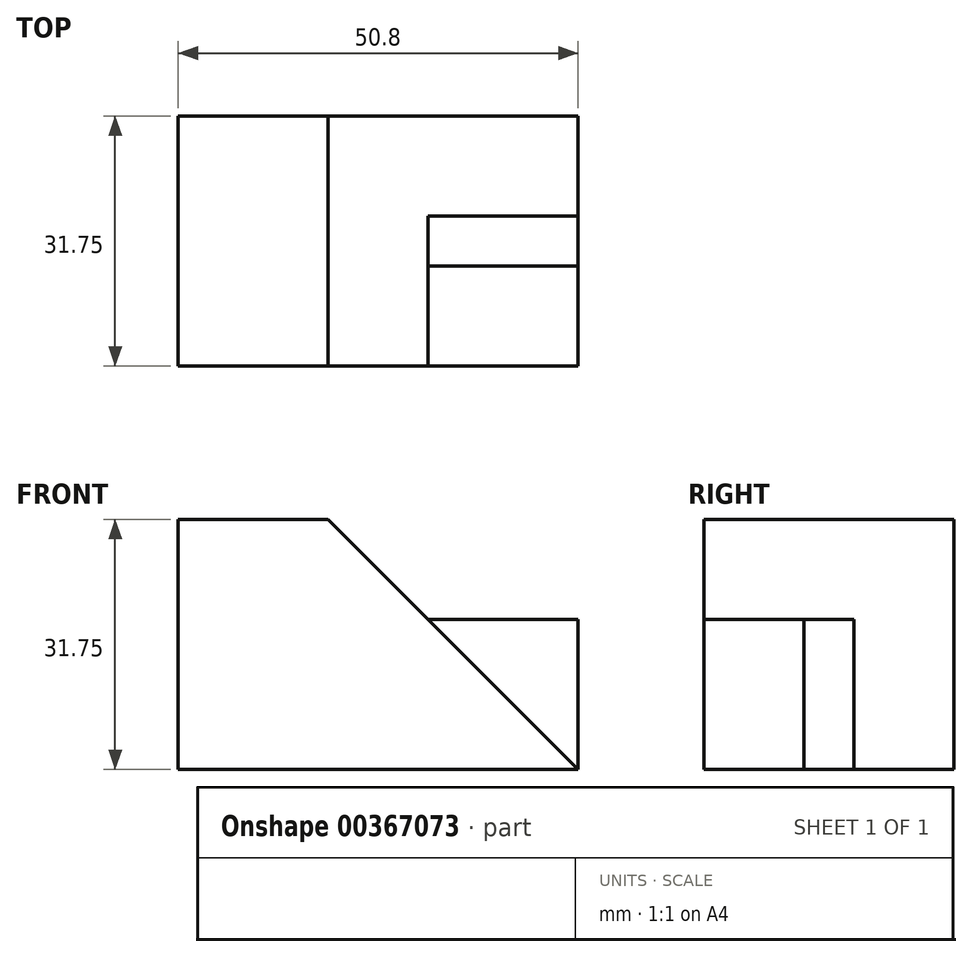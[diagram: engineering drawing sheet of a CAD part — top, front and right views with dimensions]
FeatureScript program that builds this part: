
annotation { "Feature Type Name" : "Feature", "Feature Type Description" : "" }
export const myFeature = defineFeature(function(context is Context, id is Id, definition is map)
    precondition{}
    {
        {
            var Q0;
            Q0=qCreatedBy(makeId("Front.planeOp"),FACE);
            var sketch = newSketch(context, id + "F0", { "sketchPlane" : qUnion([Q0])});
            skLineSegment(sketch, "E0", {"start": v(0, 31.75) * mm, "end": v(19.05, 31.75) * mm});
            skLineSegment(sketch, "E1", {"start": v(19.05, 31.75) * mm, "end": v(50.8, 0) * mm});
            skLineSegment(sketch, "E2", {"start": v(50.8, 0) * mm, "end": v(0, 0) * mm});
            skLineSegment(sketch, "E3", {"start": v(0, 31.75) * mm, "end": v(0, 0) * mm});
            skSolve(sketch);
        }
        {
            var Q0;
            Q0 = qSketchRegion(id + "F0", true);
            extrude(context, id + "F1", {"entities" : qUnion([Q0]), "depth" : 31.75 * mm});
        }
        {
            var Q0;
            Q0=makeQuery(id+"F1.opExtrude","CAP_FACE",FACE,{"disambiguationData":[OSD([sQuery(id+"F0.wireOp",EDGE,"E0"),sQuery(id+"F0.wireOp",EDGE,"E1"),sQuery(id+"F0.wireOp",EDGE,"E2"),sQuery(id+"F0.wireOp",EDGE,"E3")])],"isStart":false});
            var sketch = newSketch(context, id + "F2", { "sketchPlane" : qUnion([Q0])});
            skLineSegment(sketch, "E4", {"start": v(31.75, 19.05) * mm, "end": v(50.8, 19.05) * mm});
            skLineSegment(sketch, "E5", {"start": v(50.8, 19.05) * mm, "end": v(50.8, 0) * mm});
            skLineSegment(sketch, "E6", {"start": v(50.8, 0) * mm, "end": v(31.75, 19.05) * mm});
            skSolve(sketch);
        }
        {
            var Q0;
            Q0 = qSketchRegion(id + "F2", true);
            extrude(context, id + "F3", {"entities" : qUnion([Q0]), "oppositeDirection" : true, "depth" : 19.05 * mm});
        }
        {
            var Q0;
            Q0=makeQuery(id+"F3.opExtrude","CAP_FACE",FACE,{"disambiguationData":[OSD([sQuery(id+"F2.wireOp",EDGE,"E4"),sQuery(id+"F2.wireOp",EDGE,"E5"),sQuery(id+"F2.wireOp",EDGE,"E6")])],"isStart":true});
            var sketch = newSketch(context, id + "F4", { "sketchPlane" : qUnion([Q0])});
            skLineSegment(sketch, "E7", {"start": v(31.75, 19.05) * mm, "end": v(50.8, 19.05) * mm});
            skLineSegment(sketch, "E8", {"start": v(50.8, 19.05) * mm, "end": v(50.8, 0) * mm});
            skLineSegment(sketch, "E9", {"start": v(50.8, 0) * mm, "end": v(31.75, 19.05) * mm});
            skSolve(sketch);
        }
        {
            var Q0;
            Q0 = qSketchRegion(id + "F4", true);
            extrude(context, id + "F5", {"entities" : qUnion([Q0]), "oppositeDirection" : true, "depth" : 12.7 * mm});
        }
    });
